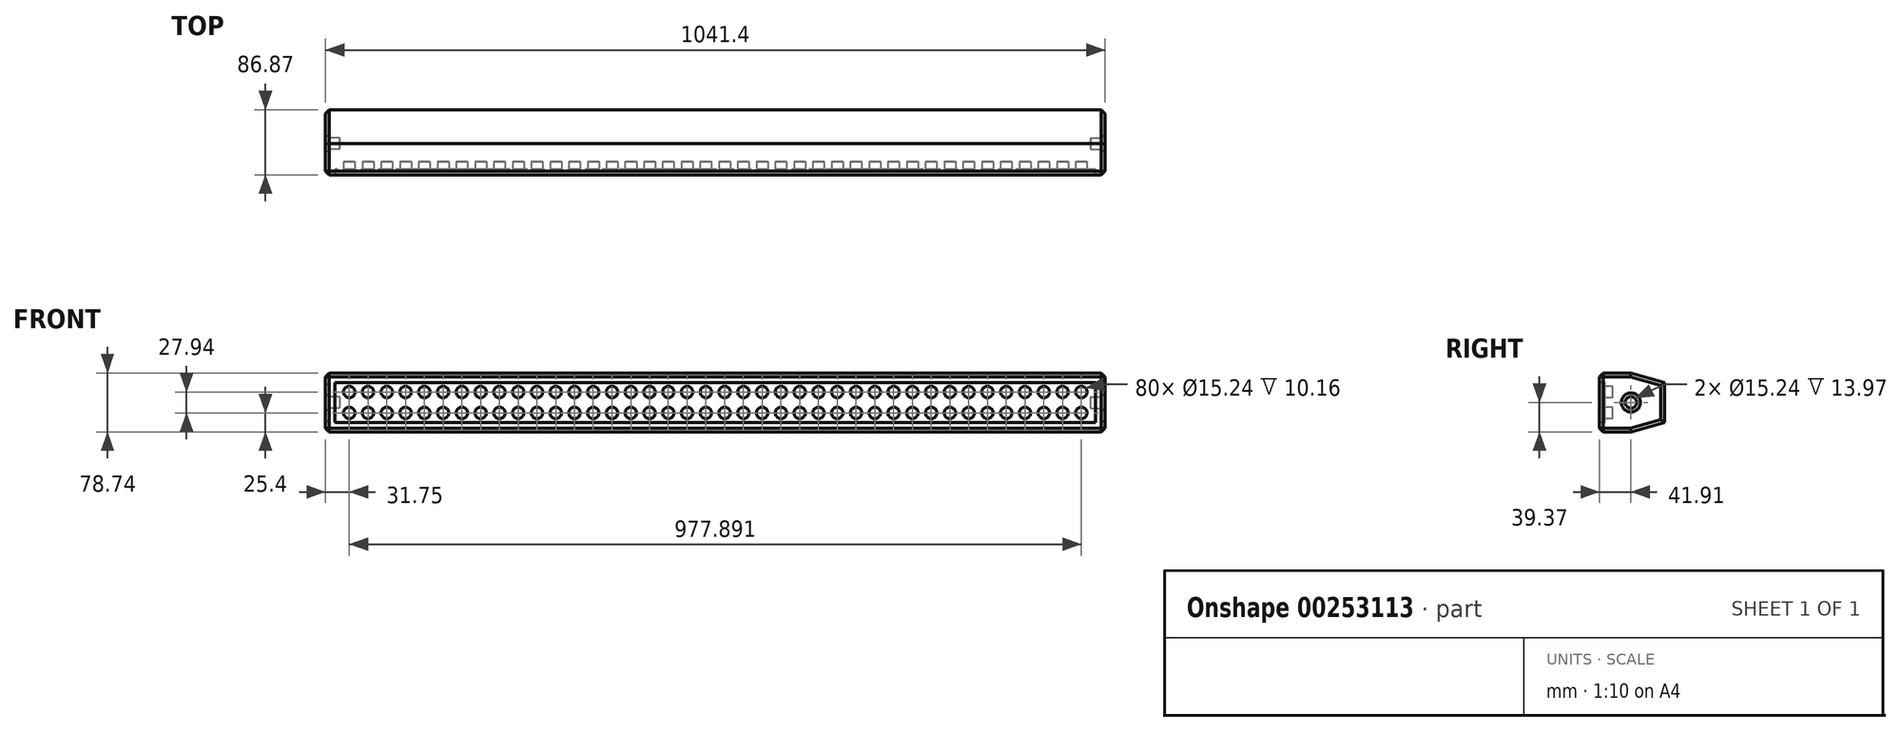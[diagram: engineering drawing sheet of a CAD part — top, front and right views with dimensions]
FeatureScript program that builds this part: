
annotation { "Feature Type Name" : "Feature", "Feature Type Description" : "" }
export const myFeature = defineFeature(function(context is Context, id is Id, definition is map)
    precondition{}
    {
        {
            var Q0;
            Q0=qCreatedBy(makeId("Right.planeOp"),FACE);
            var sketch = newSketch(context, id + "F0", { "sketchPlane" : qUnion([Q0])});
            skLineSegment(sketch, "E0", {"start": v(0, 0) * mm, "end": v(35.11, 0) * mm, "construction": true});
            skLineSegment(sketch, "E1", {"start": v(0, 39.37) * mm, "end": v(41.91, 39.37) * mm});
            skLineSegment(sketch, "E2", {"start": v(0, 39.37) * mm, "end": v(0, 0) * mm});
            skLineSegment(sketch, "E3.MirrorCS", {"start": v(0, -39.37) * mm, "end": v(41.91, -39.37) * mm});
            skLineSegment(sketch, "E4.MirrorCS", {"start": v(0, -39.37) * mm, "end": v(0, 0) * mm});
            skLineSegment(sketch, "E5", {"start": v(41.9, 39.37) * mm, "end": v(86.87, 26.67) * mm});
            skLineSegment(sketch, "E6", {"start": v(86.87, 26.67) * mm, "end": v(86.87, 0) * mm});
            skLineSegment(sketch, "E7.MirrorCS", {"start": v(-41.9, 39.37) * mm, "end": v(-86.87, 26.67) * mm});
            skLineSegment(sketch, "E8.MirrorCS", {"start": v(41.9, -39.37) * mm, "end": v(86.87, -26.67) * mm});
            skLineSegment(sketch, "E9.MirrorCS", {"start": v(86.87, -26.67) * mm, "end": v(86.87, 0) * mm});
            skSolve(sketch);
        }
        {
            var Q0;
            Q0=qSketchRegion(id+"F0",true);
            extrude(context, id + "F1", {"entities" : qUnion([Q0]), "endBound" : BoundingType.SYMMETRIC, "depth" : 1041.4 * mm});
        }
        {
            var Q0;
            Q0=makeQuery(id+"F1.opExtrude","SWEPT_FACE",FACE,{"disambiguationData":[OSD([sQuery(id+"F0.wireOp",EDGE,"E2"),sQuery(id+"F0.wireOp",EDGE,"E4.MirrorCS")])]});
            var sketch = newSketch(context, id + "F2", { "sketchPlane" : qUnion([Q0])});
            skLineSegment(sketch, "E10.bottom", {"start": v(508, -26.67) * mm, "end": v(-508, -26.67) * mm});
            skLineSegment(sketch, "E10.top", {"start": v(508, 26.67) * mm, "end": v(-508, 26.67) * mm});
            skLineSegment(sketch, "E10.left", {"start": v(508, -26.67) * mm, "end": v(508, 26.67) * mm});
            skLineSegment(sketch, "E10.right", {"start": v(-508, -26.67) * mm, "end": v(-508, 26.67) * mm});
            skPoint(sketch, "E10.middle", {"position": v(0, 0) * mm});
            skSolve(sketch);
        }
        {
            var Q0;
            Q0=qSketchRegion(id+"F2",true);
            extrude(context, id + "F3", {"entities" : qUnion([Q0]), "operationType" : NewBodyOperationType.REMOVE, "oppositeDirection" : true, "depth" : 7.62 * mm});
        }
        {
            var Q0;
            Q0=makeQuery(id+"F3.boolean.opBoolean","COPY",FACE,{"derivedFrom":makeQuery(id+"F3.opExtrude","CAP_FACE",FACE,{"disambiguationData":[OSD([sQuery(id+"F2.wireOp",EDGE,"E10.bottom"),sQuery(id+"F2.wireOp",EDGE,"E10.top"),sQuery(id+"F2.wireOp",EDGE,"E10.left"),sQuery(id+"F2.wireOp",EDGE,"E10.right")])],"isStart":false})});
            var sketch = newSketch(context, id + "F4", { "sketchPlane" : qUnion([Q0])});
            skCircle(sketch, "E11", {"center": v(-488.95, 13.97) * mm, "radius": 7.62 * mm});
            skLineSegment(sketch, "E12", {"start": v(0, 0) * mm, "end": v(-922.25, 0) * mm, "construction": true});
            skCircle(sketch, "E13.1.0.0", {"center": v(-463.88, 13.97) * mm, "radius": 7.62 * mm});
            skCircle(sketch, "E13.2.0.0", {"center": v(-438.8, 13.97) * mm, "radius": 7.62 * mm});
            skCircle(sketch, "E13.3.0.0", {"center": v(-413.73, 13.97) * mm, "radius": 7.62 * mm});
            skCircle(sketch, "E13.4.0.0", {"center": v(-388.65, 13.97) * mm, "radius": 7.62 * mm});
            skCircle(sketch, "E13.5.0.0", {"center": v(-363.58, 13.97) * mm, "radius": 7.62 * mm});
            skCircle(sketch, "E13.6.0.0", {"center": v(-338.5, 13.97) * mm, "radius": 7.62 * mm});
            skCircle(sketch, "E13.7.0.0", {"center": v(-313.43, 13.97) * mm, "radius": 7.62 * mm});
            skCircle(sketch, "E13.8.0.0", {"center": v(-288.36, 13.97) * mm, "radius": 7.62 * mm});
            skCircle(sketch, "E13.9.0.0", {"center": v(-263.28, 13.97) * mm, "radius": 7.62 * mm});
            skCircle(sketch, "E13.10.0.0", {"center": v(-238.2, 13.97) * mm, "radius": 7.62 * mm});
            skCircle(sketch, "E13.11.0.0", {"center": v(-213.13, 13.97) * mm, "radius": 7.62 * mm});
            skCircle(sketch, "E13.12.0.0", {"center": v(-188.06, 13.97) * mm, "radius": 7.62 * mm});
            skCircle(sketch, "E13.13.0.0", {"center": v(-162.99, 13.97) * mm, "radius": 7.62 * mm});
            skCircle(sketch, "E13.14.0.0", {"center": v(-137.91, 13.97) * mm, "radius": 7.62 * mm});
            skCircle(sketch, "E13.15.0.0", {"center": v(-112.84, 13.97) * mm, "radius": 7.62 * mm});
            skCircle(sketch, "E13.16.0.0", {"center": v(-87.76, 13.97) * mm, "radius": 7.62 * mm});
            skCircle(sketch, "E13.17.0.0", {"center": v(-62.7, 13.97) * mm, "radius": 7.62 * mm});
            skCircle(sketch, "E13.18.0.0", {"center": v(-37.62, 13.97) * mm, "radius": 7.62 * mm});
            skCircle(sketch, "E13.19.0.0", {"center": v(-12.54, 13.97) * mm, "radius": 7.62 * mm});
            skCircle(sketch, "E13.20.0.0", {"center": v(12.53, 13.97) * mm, "radius": 7.62 * mm});
            skCircle(sketch, "E13.21.0.0", {"center": v(37.6, 13.97) * mm, "radius": 7.62 * mm});
            skCircle(sketch, "E13.22.0.0", {"center": v(62.68, 13.97) * mm, "radius": 7.62 * mm});
            skCircle(sketch, "E13.23.0.0", {"center": v(87.75, 13.97) * mm, "radius": 7.62 * mm});
            skCircle(sketch, "E13.24.0.0", {"center": v(112.83, 13.97) * mm, "radius": 7.62 * mm});
            skCircle(sketch, "E13.25.0.0", {"center": v(137.9, 13.97) * mm, "radius": 7.62 * mm});
            skCircle(sketch, "E13.26.0.0", {"center": v(162.98, 13.97) * mm, "radius": 7.62 * mm});
            skCircle(sketch, "E13.27.0.0", {"center": v(188.05, 13.97) * mm, "radius": 7.62 * mm});
            skCircle(sketch, "E13.28.0.0", {"center": v(213.13, 13.97) * mm, "radius": 7.62 * mm});
            skCircle(sketch, "E13.29.0.0", {"center": v(238.2, 13.97) * mm, "radius": 7.62 * mm});
            skCircle(sketch, "E13.30.0.0", {"center": v(263.27, 13.97) * mm, "radius": 7.62 * mm});
            skCircle(sketch, "E13.31.0.0", {"center": v(288.35, 13.97) * mm, "radius": 7.62 * mm});
            skCircle(sketch, "E13.32.0.0", {"center": v(313.42, 13.97) * mm, "radius": 7.62 * mm});
            skCircle(sketch, "E13.33.0.0", {"center": v(338.5, 13.97) * mm, "radius": 7.62 * mm});
            skCircle(sketch, "E13.34.0.0", {"center": v(363.57, 13.97) * mm, "radius": 7.62 * mm});
            skCircle(sketch, "E13.35.0.0", {"center": v(388.64, 13.97) * mm, "radius": 7.62 * mm});
            skCircle(sketch, "E13.36.0.0", {"center": v(413.72, 13.97) * mm, "radius": 7.62 * mm});
            skCircle(sketch, "E13.37.0.0", {"center": v(438.8, 13.97) * mm, "radius": 7.62 * mm});
            skCircle(sketch, "E13.38.0.0", {"center": v(463.87, 13.97) * mm, "radius": 7.62 * mm});
            skCircle(sketch, "E13.39.0.0", {"center": v(488.94, 13.97) * mm, "radius": 7.62 * mm});
            skLineSegment(sketch, "E13.direction1", {"start": v(-488.95, 13.97) * mm, "end": v(-463.88, 13.97) * mm, "construction": true});
            skCircle(sketch, "E14.MirrorC", {"center": v(488.94, -13.97) * mm, "radius": 7.62 * mm});
            skCircle(sketch, "E15.MirrorC", {"center": v(-413.73, -13.97) * mm, "radius": 7.62 * mm});
            skCircle(sketch, "E16.MirrorC", {"center": v(-313.43, -13.97) * mm, "radius": 7.62 * mm});
            skCircle(sketch, "E17.MirrorC", {"center": v(12.53, -13.97) * mm, "radius": 7.62 * mm});
            skCircle(sketch, "E18.MirrorC", {"center": v(-37.62, -13.97) * mm, "radius": 7.62 * mm});
            skCircle(sketch, "E19.MirrorC", {"center": v(-87.76, -13.97) * mm, "radius": 7.62 * mm});
            skCircle(sketch, "E20.MirrorC", {"center": v(-388.65, -13.97) * mm, "radius": 7.62 * mm});
            skCircle(sketch, "E21.MirrorC", {"center": v(413.72, -13.97) * mm, "radius": 7.62 * mm});
            skCircle(sketch, "E22.MirrorC", {"center": v(363.57, -13.97) * mm, "radius": 7.62 * mm});
            skCircle(sketch, "E23.MirrorC", {"center": v(313.42, -13.97) * mm, "radius": 7.62 * mm});
            skCircle(sketch, "E24.MirrorC", {"center": v(-288.36, -13.97) * mm, "radius": 7.62 * mm});
            skCircle(sketch, "E25.MirrorC", {"center": v(-488.95, -13.97) * mm, "radius": 7.62 * mm});
            skCircle(sketch, "E26.MirrorC", {"center": v(238.2, -13.97) * mm, "radius": 7.62 * mm});
            skCircle(sketch, "E27.MirrorC", {"center": v(162.98, -13.97) * mm, "radius": 7.62 * mm});
            skCircle(sketch, "E28.MirrorC", {"center": v(62.68, -13.97) * mm, "radius": 7.62 * mm});
            skCircle(sketch, "E29.MirrorC", {"center": v(-363.58, -13.97) * mm, "radius": 7.62 * mm});
            skCircle(sketch, "E30.MirrorC", {"center": v(112.83, -13.97) * mm, "radius": 7.62 * mm});
            skCircle(sketch, "E31.MirrorC", {"center": v(-263.28, -13.97) * mm, "radius": 7.62 * mm});
            skCircle(sketch, "E32.MirrorC", {"center": v(-188.06, -13.97) * mm, "radius": 7.62 * mm});
            skLineSegment(sketch, "E33.MirrorCS", {"start": v(-488.95, -13.97) * mm, "end": v(-463.88, -13.97) * mm, "construction": true});
            skCircle(sketch, "E34.MirrorC", {"center": v(463.87, -13.97) * mm, "radius": 7.62 * mm});
            skCircle(sketch, "E35.MirrorC", {"center": v(-238.2, -13.97) * mm, "radius": 7.62 * mm});
            skCircle(sketch, "E36.MirrorC", {"center": v(-463.88, -13.97) * mm, "radius": 7.62 * mm});
            skCircle(sketch, "E37.MirrorC", {"center": v(37.6, -13.97) * mm, "radius": 7.62 * mm});
            skCircle(sketch, "E38.MirrorC", {"center": v(-162.99, -13.97) * mm, "radius": 7.62 * mm});
            skCircle(sketch, "E39.MirrorC", {"center": v(-62.7, -13.97) * mm, "radius": 7.62 * mm});
            skCircle(sketch, "E40.MirrorC", {"center": v(-112.84, -13.97) * mm, "radius": 7.62 * mm});
            skCircle(sketch, "E41.MirrorC", {"center": v(-12.54, -13.97) * mm, "radius": 7.62 * mm});
            skCircle(sketch, "E42.MirrorC", {"center": v(438.8, -13.97) * mm, "radius": 7.62 * mm});
            skCircle(sketch, "E43.MirrorC", {"center": v(388.64, -13.97) * mm, "radius": 7.62 * mm});
            skCircle(sketch, "E44.MirrorC", {"center": v(338.5, -13.97) * mm, "radius": 7.62 * mm});
            skCircle(sketch, "E45.MirrorC", {"center": v(288.35, -13.97) * mm, "radius": 7.62 * mm});
            skCircle(sketch, "E46.MirrorC", {"center": v(213.13, -13.97) * mm, "radius": 7.62 * mm});
            skCircle(sketch, "E47.MirrorC", {"center": v(263.27, -13.97) * mm, "radius": 7.62 * mm});
            skCircle(sketch, "E48.MirrorC", {"center": v(-213.13, -13.97) * mm, "radius": 7.62 * mm});
            skCircle(sketch, "E49.MirrorC", {"center": v(-438.8, -13.97) * mm, "radius": 7.62 * mm});
            skCircle(sketch, "E50.MirrorC", {"center": v(-137.91, -13.97) * mm, "radius": 7.62 * mm});
            skCircle(sketch, "E51.MirrorC", {"center": v(-338.5, -13.97) * mm, "radius": 7.62 * mm});
            skCircle(sketch, "E52.MirrorC", {"center": v(137.9, -13.97) * mm, "radius": 7.62 * mm});
            skCircle(sketch, "E53.MirrorC", {"center": v(87.75, -13.97) * mm, "radius": 7.62 * mm});
            skCircle(sketch, "E54.MirrorC", {"center": v(188.05, -13.97) * mm, "radius": 7.62 * mm});
            skSolve(sketch);
        }
        {
            var Q0;
            Q0=qSketchRegion(id+"F4",true);
            extrude(context, id + "F5", {"entities" : qUnion([Q0]), "operationType" : NewBodyOperationType.REMOVE, "oppositeDirection" : true, "depth" : 10.16 * mm});
        }
        {
            var Q0;
            Q0=makeQuery(id+"F1.opExtrude","CAP_FACE",FACE,{"disambiguationData":[OSD([sQuery(id+"F0.wireOp",EDGE,"E1"),sQuery(id+"F0.wireOp",EDGE,"E2"),sQuery(id+"F0.wireOp",EDGE,"E3.MirrorCS"),sQuery(id+"F0.wireOp",EDGE,"E4.MirrorCS"),sQuery(id+"F0.wireOp",EDGE,"a03aa2aa-5a6f-4576-b362-bd34c7c2a79d.trimOffspring")])],"isStart":false});
            var sketch = newSketch(context, id + "F6", { "sketchPlane" : qUnion([Q0])});
            skCircle(sketch, "E55", {"center": v(41.91, 0) * mm, "radius": 7.62 * mm});
            skLineSegment(sketch, "E56", {"start": v(41.91, 39.37) * mm, "end": v(41.91, -39.37) * mm, "construction": true});
            skSolve(sketch);
        }
        {
            var Q0;
            Q0=qSketchRegion(id+"F6",true);
            extrude(context, id + "F7", {"entities" : qUnion([Q0]), "operationType" : NewBodyOperationType.REMOVE, "oppositeDirection" : true, "depth" : 19.05 * mm});
        }
        {
            var Q0;
            Q0=makeQuery(id+"F1.opExtrude","CAP_FACE",FACE,{"disambiguationData":[OSD([sQuery(id+"F0.wireOp",EDGE,"E1"),sQuery(id+"F0.wireOp",EDGE,"E2"),sQuery(id+"F0.wireOp",EDGE,"E3.MirrorCS"),sQuery(id+"F0.wireOp",EDGE,"E4.MirrorCS"),sQuery(id+"F0.wireOp",EDGE,"a03aa2aa-5a6f-4576-b362-bd34c7c2a79d.trimOffspring")])],"isStart":true});
            var sketch = newSketch(context, id + "F8", { "sketchPlane" : qUnion([Q0])});
            skCircle(sketch, "E57", {"center": v(-41.91, 0) * mm, "radius": 7.62 * mm});
            skLineSegment(sketch, "E58", {"start": v(-41.91, 39.37) * mm, "end": v(-41.91, -39.37) * mm, "construction": true});
            skSolve(sketch);
        }
        {
            var Q0;
            Q0=qSketchRegion(id+"F8",true);
            extrude(context, id + "F9", {"entities" : qUnion([Q0]), "operationType" : NewBodyOperationType.REMOVE, "oppositeDirection" : true, "depth" : 19.05 * mm});
        }
        {
            var Q0;
            Q0=makeQuery(id+"F1.opExtrude","CAP_FACE",FACE,{"disambiguationData":[OSD([sQuery(id+"F0.wireOp",EDGE,"E1"),sQuery(id+"F0.wireOp",EDGE,"E2"),sQuery(id+"F0.wireOp",EDGE,"E3.MirrorCS"),sQuery(id+"F0.wireOp",EDGE,"E4.MirrorCS"),sQuery(id+"F0.wireOp",EDGE,"a03aa2aa-5a6f-4576-b362-bd34c7c2a79d.trimOffspring")])],"isStart":true});
            var Q1;
            Q1=makeQuery(id+"F1.opExtrude","CAP_FACE",FACE,{"disambiguationData":[OSD([sQuery(id+"F0.wireOp",EDGE,"E1"),sQuery(id+"F0.wireOp",EDGE,"E2"),sQuery(id+"F0.wireOp",EDGE,"E3.MirrorCS"),sQuery(id+"F0.wireOp",EDGE,"E4.MirrorCS"),sQuery(id+"F0.wireOp",EDGE,"a03aa2aa-5a6f-4576-b362-bd34c7c2a79d.trimOffspring")])],"isStart":false});
            var Q2;
            Q2=makeQuery(id+"F1.opExtrude","SWEPT_EDGE",EDGE,{"disambiguationData":[OSD([sQuery(id+"F0.wireOp",EDGE,"E1"),sQuery(id+"F0.wireOp",EDGE,"E2")])]});
            var Q3;
            Q3=makeQuery(id+"F1.opExtrude","SWEPT_EDGE",EDGE,{"disambiguationData":[OSD([sQuery(id+"F0.wireOp",EDGE,"E3.MirrorCS"),sQuery(id+"F0.wireOp",EDGE,"E4.MirrorCS")])]});
            chamfer(context, id + "F10", {"entities" : qUnion([Q0, Q1, Q2, Q3]), "width" : 5.08 * mm, "tangentPropagation" : true});
        }
    });
